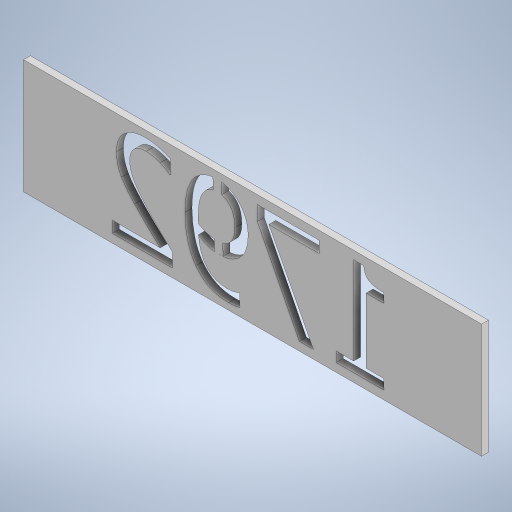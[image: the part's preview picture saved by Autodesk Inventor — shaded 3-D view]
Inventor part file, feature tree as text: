
AUTODESK INVENTOR PART (.ipt)
format: ipt  version: 2023.4 (Build 274418000, 418)  size: 414,720 bytes
history: native  units: in
note: dims shown in document units (in); Inventor stores cm internally (conversion verified against a paired STEP export)
features: sketch x3, projected_geometry x3, extrude x2, sheet_metal_op x1, other x1
ambient origin geometry x8: Origin, YZ Plane, XZ Plane, XY Plane, X Axis, Y Axis, Z Axis, Center Point
bodies: Solid1 (feature_tree)
feature tree (10):
  sheet_metal_op  "Face1"
  extrude  "Extrusion1"  Depth=2.0in
  extrude  "Extrusion2"  Depth=1.0in TaperAngle=0.0deg
  sketch  "Sketch1"  dims[d0=8.0in d1=2.0in]
  other  "Plate1"
  sketch  "Sketch2"  dims[d2=0.12in d3=1.0in d4=0.0in]
  projected_geometry  "Projected Loop1"
  sketch  "Sketch3"  dims[d5=0.1505in d6=0.2746in d7=0.3986in d8=1.0in d9=0.0in]
  projected_geometry  "Projected Loop2"
  projected_geometry  "Projected Loop3"
